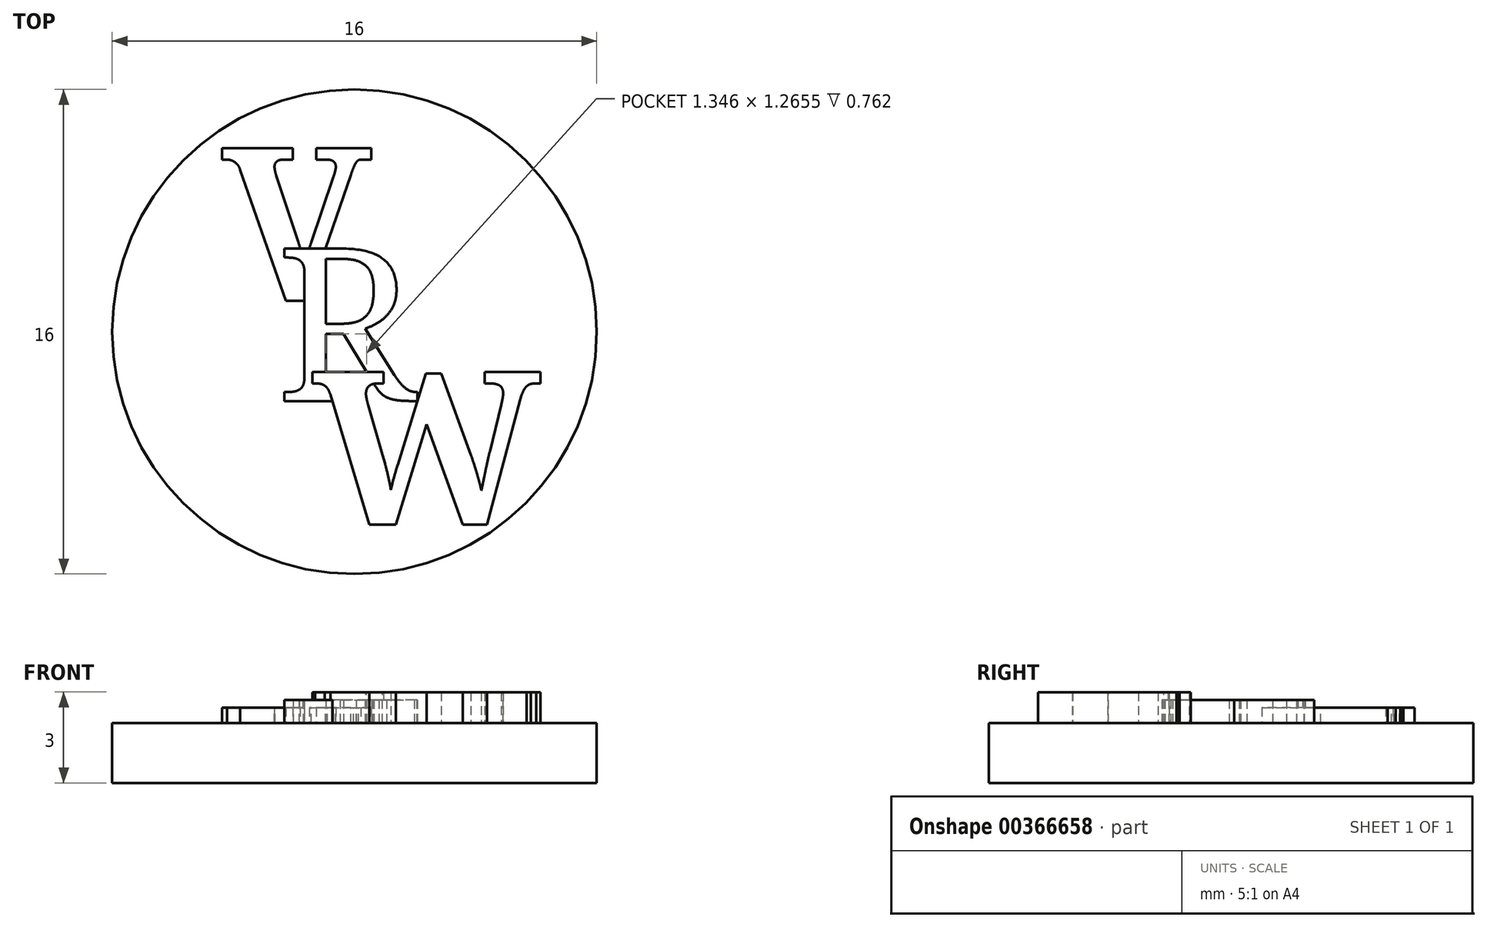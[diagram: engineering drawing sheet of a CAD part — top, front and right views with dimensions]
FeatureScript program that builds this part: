
annotation { "Feature Type Name" : "Feature", "Feature Type Description" : "" }
export const myFeature = defineFeature(function(context is Context, id is Id, definition is map)
    precondition{}
    {
        {
            var Q0;
            Q0=qCreatedBy(makeId("Top.planeOp"),FACE);
            var sketch = newSketch(context, id + "F0", { "sketchPlane" : qUnion([Q0])});
            skCircle(sketch, "E0", {"center": v(0, 0) * mm, "radius": 8 * mm});
            skSolve(sketch);
        }
        {
            var Q0;
            Q0 = qSketchRegion(id + "F0", true);
            extrude(context, id + "F1", {"entities" : qUnion([Q0]), "depth" : 1.98 * mm});
        }
        {
            var Q0;
            Q0=makeQuery(id+"F1.opExtrude","CAP_FACE",FACE,{"disambiguationData":[OSD([sQuery(id+"F0.wireOp",EDGE,"E0")])],"isStart":false});
            var sketch = newSketch(context, id + "F2", { "sketchPlane" : qUnion([Q0])});
            skText(sketch, "E1", { "text": "V", "fontName": "NotoSerif-Bold.ttf"});
            const initialGuessF2  = {"E1": [-0.00437, 0.00102, 1, 0, 0.00508]};
            skSetInitialGuess(sketch, initialGuessF2);
            skSolve(sketch);
        }
        {
            var Q0;
            Q0=makeQuery(id+"F2.imprint","IMPRINT",FACE,{"disambiguationData":[TD([[makeQuery(id+"F2.imprint","IMPRINT",EDGE,{"derivedFrom":sQuery(id+"F2.wireOp",EDGE,"E1.sketch_text.stroke-0")}),1.0]])]});
            var sketch = newSketch(context, id + "F3", { "sketchPlane" : qUnion([Q0])});
            skText(sketch, "E2", { "text": "R", "fontName": "NotoSerif-Regular.ttf"});
            const initialGuessF3  = {"E2": [-0.00259, -0.00229, 1, 0, 0.00508]};
            skSetInitialGuess(sketch, initialGuessF3);
            skSolve(sketch);
        }
        {
            var Q0;
            Q0=makeQuery(id+"F2.imprint","IMPRINT",FACE,{"disambiguationData":[TD([[makeQuery(id+"F2.imprint","IMPRINT",EDGE,{"derivedFrom":sQuery(id+"F2.wireOp",EDGE,"E1.sketch_text.stroke-0")}),1.0]])]});
            var sketch = newSketch(context, id + "F4", { "sketchPlane" : qUnion([Q0])});
            skText(sketch, "E3", { "text": "W", "fontName": "NotoSerif-Bold.ttf"});
            const initialGuessF4  = {"E3": [-0.00139, -0.00637, 1, 0, 0.00508]};
            skSetInitialGuess(sketch, initialGuessF4);
            skSolve(sketch);
        }
        {
            var Q0;
            Q0 = qSketchRegion(id + "F2", true);
            extrude(context, id + "F5", {"entities" : qUnion([Q0]), "operationType" : NewBodyOperationType.ADD, "depth" : 0.5 * mm});
        }
        {
            var Q0;
            Q0 = qSketchRegion(id + "F3", true);
            extrude(context, id + "F6", {"entities" : qUnion([Q0]), "operationType" : NewBodyOperationType.ADD, "depth" : 0.76 * mm});
        }
        {
            var Q0;
            Q0 = qSketchRegion(id + "F4", true);
            extrude(context, id + "F7", {"entities" : qUnion([Q0]), "operationType" : NewBodyOperationType.ADD, "depth" : 1.02 * mm});
        }
    });
